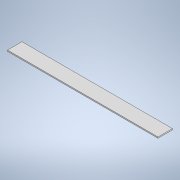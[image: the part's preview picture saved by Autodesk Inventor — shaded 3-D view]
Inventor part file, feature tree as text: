
AUTODESK INVENTOR PART (.ipt)
format: ipt  version: 2020.1 (Build 241239000, 239)  size: 95,744 bytes
history: native  units: mm
features: other x1, extrude x1, sketch x1
ambient origin geometry x8: Origin, YZ Plane, XZ Plane, XY Plane, X Axis, Y Axis, Z Axis, Center Point
bodies: Body1 (feature_tree)
feature tree (3):
  other  "Твердое тело1"
  extrude  "Выдавливание1"  Depth=96.0mm
  sketch  "Эскиз1"
